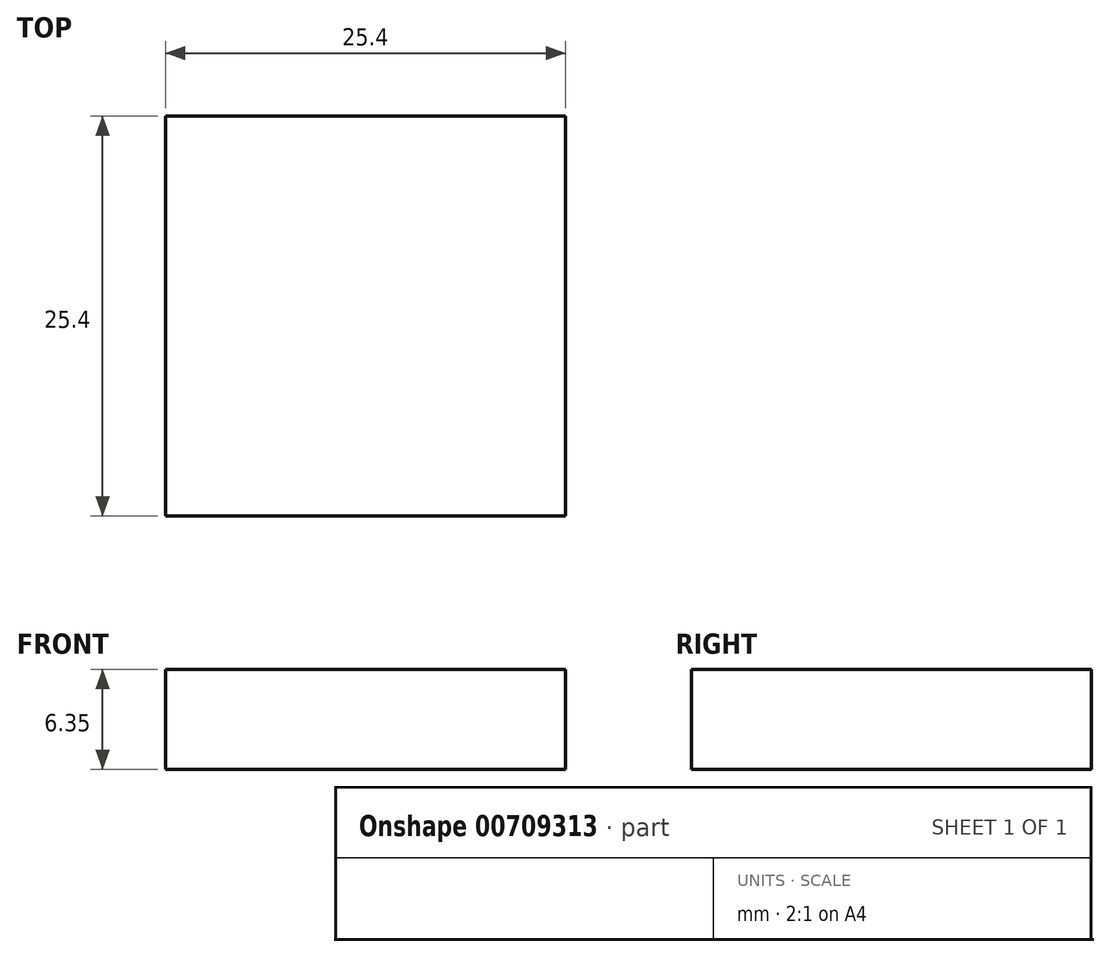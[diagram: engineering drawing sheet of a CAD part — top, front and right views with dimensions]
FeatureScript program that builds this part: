
annotation { "Feature Type Name" : "Feature", "Feature Type Description" : "" }
export const myFeature = defineFeature(function(context is Context, id is Id, definition is map)
    precondition{}
    {
        {
            var Q0;
            Q0=qCreatedBy(makeId("Top.planeOp"),FACE);
            var sketch = newSketch(context, id + "F0", { "sketchPlane" : qUnion([Q0])});
            skLineSegment(sketch, "E0.bottom", {"start": v(12.7, 12.7) * mm, "end": v(-12.7, 12.7) * mm});
            skLineSegment(sketch, "E0.top", {"start": v(12.7, -12.7) * mm, "end": v(-12.7, -12.7) * mm});
            skLineSegment(sketch, "E0.left", {"start": v(12.7, 12.7) * mm, "end": v(12.7, -12.7) * mm});
            skLineSegment(sketch, "E0.right", {"start": v(-12.7, 12.7) * mm, "end": v(-12.7, -12.7) * mm});
            skPoint(sketch, "E0.middle", {"position": v(0, 0) * mm});
            skSolve(sketch);
        }
        {
            var Q0;
            Q0=makeQuery(id+"F0.imprint","IMPRINT",FACE,{"disambiguationData":[TD([[makeQuery(id+"F0.imprint","IMPRINT",EDGE,{"derivedFrom":sQuery(id+"F0.wireOp",EDGE,"E0.bottom")}),1.0]])]});
            extrude(context, id + "F1", {"entities" : qUnion([Q0]), "depth" : 6.35 * mm, "offsetDistance" : 25 * mm});
        }
    });
